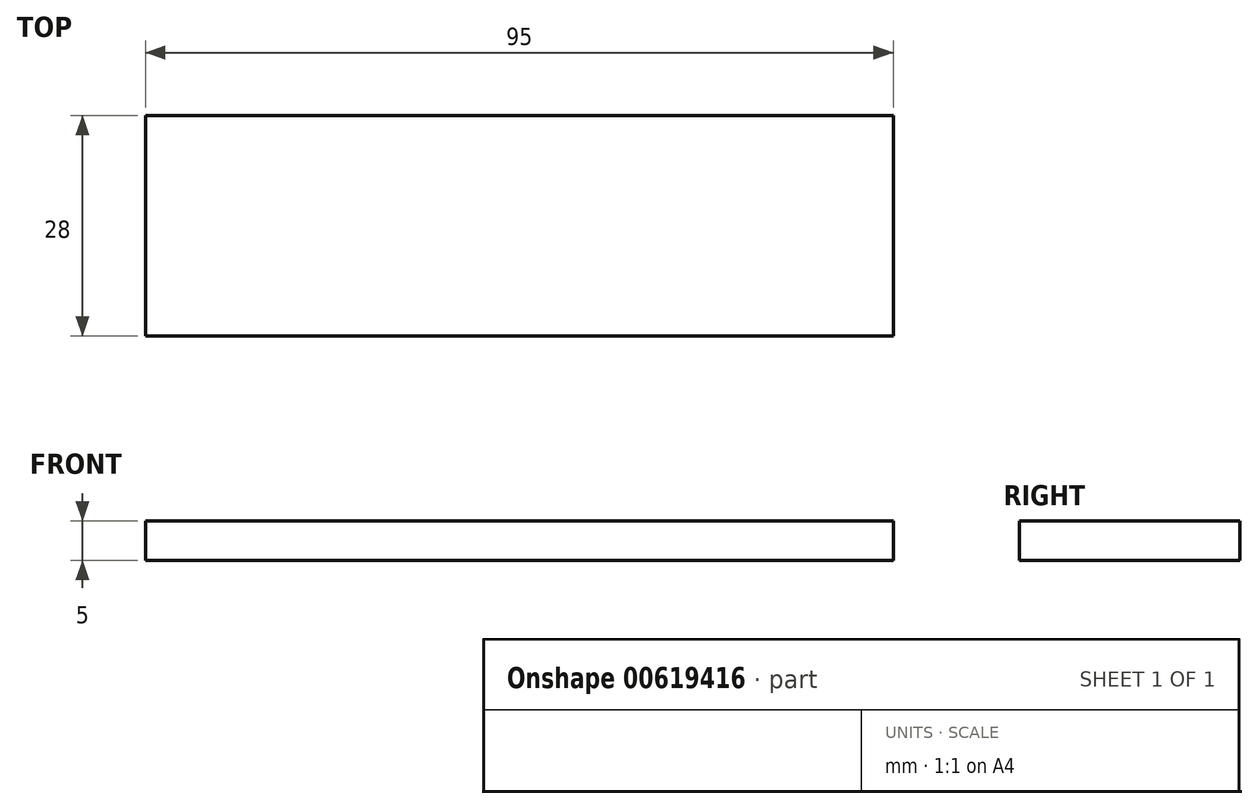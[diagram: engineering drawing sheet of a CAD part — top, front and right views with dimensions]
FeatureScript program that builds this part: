
annotation { "Feature Type Name" : "Feature", "Feature Type Description" : "" }
export const myFeature = defineFeature(function(context is Context, id is Id, definition is map)
    precondition{}
    {
        {
            var Q0;
            Q0=qCreatedBy(makeId("Top.planeOp"),FACE);
            var sketch = newSketch(context, id + "F0", { "sketchPlane" : qUnion([Q0])});
            skLineSegment(sketch, "E0.bottom", {"start": v(47.5, 14) * mm, "end": v(-47.5, 14) * mm});
            skLineSegment(sketch, "E0.top", {"start": v(47.5, -14) * mm, "end": v(-47.5, -14) * mm});
            skLineSegment(sketch, "E0.left", {"start": v(47.5, 14) * mm, "end": v(47.5, -14) * mm});
            skLineSegment(sketch, "E0.right", {"start": v(-47.5, 14) * mm, "end": v(-47.5, -14) * mm});
            skPoint(sketch, "E0.middle", {"position": v(0, 0) * mm});
            skSolve(sketch);
        }
        {
            var Q0;
            Q0 = qSketchRegion(id + "F0", true);
            extrude(context, id + "F1", {"entities" : qUnion([Q0]), "depth" : 5 * mm, "offsetDistance" : 25 * mm});
        }
    });
